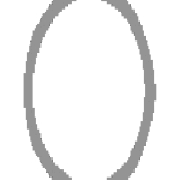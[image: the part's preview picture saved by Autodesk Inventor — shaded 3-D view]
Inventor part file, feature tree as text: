
AUTODESK INVENTOR PART (.ipt)
format: ipt  version: 2021 (Build 250183000, 183)  size: 113,664 bytes
history: native  units: in
note: dims shown in document units (in); Inventor stores cm internally (conversion verified against a paired STEP export)
features: other x4, sketch x3, plane x1
ambient origin geometry x8: Origin, YZ Plane, XZ Plane, XY Plane, X Axis, Y Axis, Z Axis, Center Point
bodies: Solid1 (feature_tree), Body (feature_tree)
feature tree (8):
  other  "Driven Length"
  other  "Frame Generator"
  other  "Start Plane"
  other  "End Plane"
  sketch  "Sketch"  dims[d2=11.5in d4=-0.0in d5=11.5in d6=0.12in d7=0.0in d8=90.0deg d9=11.5in]
  sketch  "Sketch2"  dims[d0=1.0in]
  plane  "Work Plane3"
  sketch  "Sketch3"  dims[d1=0.065in]
